# Revit family: silica_r__21_51mx23tctaw_ef5e
name_source: partatom
category: Lighting Fixtures
units: mm (PartAtom-declared; Revit-internal decimal feet)

## family parameters
Cut with Voids When Loaded = No
Host = Face
Light Source = No
Part Type = Normal
Room Calculation Point = No
Round Connector Dimension = Use Diameter
Shared = No

## types (1)
- --- (1 x LED, 8070 lm, 81.1 W, 6500K)
    Apparent Load = 81 VA
    CIE Flux Codes = 78 96 99 100 100
    Color Rendering = 80
    Color Temperature = 6500K
    Default Elevation = 1800 mm
    Description = Silica® 21, office luminaire, primary optical cover: prismatic diffuser, of PMMA, CAT 2 (L<= 3000cd/m²), light emission: direct distribution, primary light characteristic: symmetric, installation type: surface-mounted, LED, rated luminous flux: 8.070lm, luminous efficacy: 95lm/W, light colour: 8tw, colour temperature: 2700..6500K, control gear: DALI DT8, with terminal, 3+2-pole, max. 2.5mm², mains connection: 220..240V, AC, 50/60Hz, rated input power: 85.1W, luminaire housing, of aluminium, traffic white (RAL 9016), length: 3.004mm, width: 53mm, height: 53mm, protection rating (complete): IP20, insulation class (complete): insulation class I (protective earthing), certification: CE, permissible operating ambient temperature: 0..+35°C, standard: EN 50419, packaging unit: 1 piece
    Height = 53 mm
    Lamp = 1 x LED
    Lamp Light Flux = 8070 lm
    Lamp Power = 81.1 W
    Lamp count = 1
    Length = 3004 mm
    Luminous efficacy = 100 lm/W
    Manufacturer = Siteco
    ModVariant = No
    Model = 51MX23TCTAW
    Mounting Place = Ceiling
    Mounting Type = Surface mounted
    Number of Poles = 1
    OnlyDefault = Yes
    Power Factor = 1
    Product Name = Silica® 21
    Product group = office luminaire | ceiling mounted
    ProductGroupID = 303
    Protection Class = Protection class I
    Protection Degree = IP 20
    RLX_Detail_Level = 1
    RLX_Emergency_Light_Flux = 0 lm
    RLX_Emergency_Type = 0
    RLX_Emergency_Type_DB = No
    RlxData = <blob elided: 15437 chars, md5=71765b76>
    Socket = socket
    Standby Power = 0 W
    System Light Flux = 8070 lm
    System Power = 81 W
    Type Comments = individual setting
    Type Image = l_1335877.jpg
    URL = http://relux.com
    VarID = @adj_161303
    Voltage = 0 V
    Weight = 0.00 kg
    Width = 53 mm

## geometry (parser evidence)
native form markers: Blend x4, Sweep x14
no freeform markers — native parametric forms only
